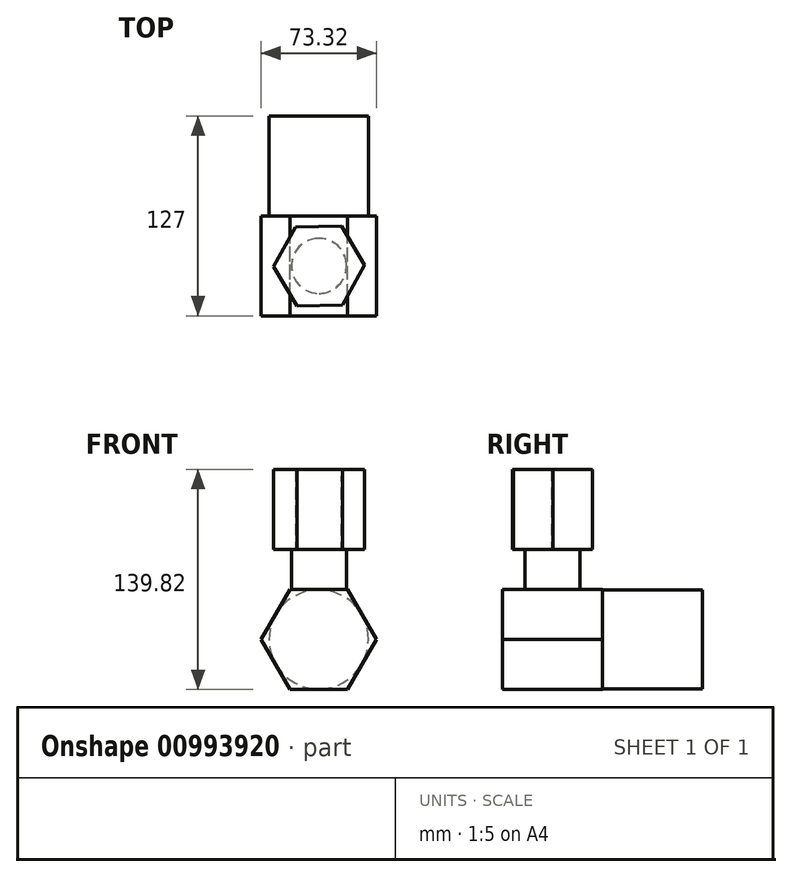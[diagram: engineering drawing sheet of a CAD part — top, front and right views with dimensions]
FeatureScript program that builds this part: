
annotation { "Feature Type Name" : "Feature", "Feature Type Description" : "" }
export const myFeature = defineFeature(function(context is Context, id is Id, definition is map)
    precondition{}
    {
        {
            var Q0;
            Q0=qCreatedBy(makeId("Front.planeOp"),FACE);
            var sketch = newSketch(context, id + "F0", { "sketchPlane" : qUnion([Q0])});
            skCircle(sketch, "E0.cCircle", {"center": v(0, 0) * mm, "radius": 31.75 * mm, "construction": true});
            skLineSegment(sketch, "E0.0", {"start": v(36.66, -0.1) * mm, "end": v(18.25, -31.8) * mm});
            skLineSegment(sketch, "E0.1", {"start": v(18.25, -31.8) * mm, "end": v(-18.4, -31.7) * mm});
            skLineSegment(sketch, "E0.2", {"start": v(-18.4, -31.7) * mm, "end": v(-36.66, 0.1) * mm});
            skLineSegment(sketch, "E0.3", {"start": v(-36.66, 0.1) * mm, "end": v(-18.25, 31.8) * mm});
            skLineSegment(sketch, "E0.4", {"start": v(-18.25, 31.8) * mm, "end": v(18.4, 31.7) * mm});
            skLineSegment(sketch, "E0.5", {"start": v(18.4, 31.7) * mm, "end": v(36.66, -0.1) * mm});
            skPoint(sketch, "E0.0.midPoint", {"position": v(27.46, -15.94) * mm});
            skSolve(sketch);
        }
        {
            var Q0;
            Q0 = qSketchRegion(id + "F0", true);
            extrude(context, id + "F1", {"entities" : qUnion([Q0]), "depth" : 63.5 * mm, "offsetDistance" : 25.4 * mm});
        }
        {
            var Q0;
            Q0=makeQuery(id+"F1.opExtrude","CAP_FACE",FACE,{"disambiguationData":[OSD([sQuery(id+"F0.wireOp",EDGE,"E0.0"),sQuery(id+"F0.wireOp",EDGE,"E0.1"),sQuery(id+"F0.wireOp",EDGE,"E0.2"),sQuery(id+"F0.wireOp",EDGE,"E0.3"),sQuery(id+"F0.wireOp",EDGE,"E0.4"),sQuery(id+"F0.wireOp",EDGE,"E0.5")])],"isStart":true});
            var sketch = newSketch(context, id + "F2", { "sketchPlane" : qUnion([Q0])});
            skCircle(sketch, "E1", {"center": v(0, 0) * mm, "radius": 31.51 * mm});
            skSolve(sketch);
        }
        {
            var Q0;
            Q0 = qSketchRegion(id + "F2", true);
            extrude(context, id + "F3", {"entities" : qUnion([Q0]), "operationType" : NewBodyOperationType.ADD, "depth" : 63.5 * mm, "offsetDistance" : 25.4 * mm});
        }
        {
            var Q0;
            Q0=makeQuery(id+"F1.opExtrude","SWEPT_FACE",FACE,{"disambiguationData":[OSD([sQuery(id+"F0.wireOp",EDGE,"E0.4")])]});
            var sketch = newSketch(context, id + "F4", { "sketchPlane" : qUnion([Q0])});
            skCircle(sketch, "E2", {"center": v(0, -31.75) * mm, "radius": 17.53 * mm});
            skPoint(sketch, "E2.centerSnap0", {"position": v(-18.33, -31.75) * mm});
            skPoint(sketch, "E2.centerSnap1", {"position": v(0, 0) * mm});
            skSolve(sketch);
        }
        {
            var Q0;
            Q0 = qSketchRegion(id + "F4", true);
            extrude(context, id + "F5", {"entities" : qUnion([Q0]), "operationType" : NewBodyOperationType.ADD, "depth" : 25.4 * mm, "offsetDistance" : 25.4 * mm});
        }
        {
            var Q0;
            Q0=makeQuery(id+"F5.opExtrude","CAP_FACE",FACE,{"disambiguationData":[OSD([sQuery(id+"F4.wireOp",EDGE,"E2")])],"isStart":false});
            var sketch = newSketch(context, id + "F6", { "sketchPlane" : qUnion([Q0])});
            skCircle(sketch, "E3.cCircle", {"center": v(0, -31.75) * mm, "radius": 25.06 * mm, "construction": true});
            skLineSegment(sketch, "E3.0", {"start": v(28.94, -31.26) * mm, "end": v(14.9, -56.56) * mm});
            skLineSegment(sketch, "E3.1", {"start": v(14.9, -56.56) * mm, "end": v(-14.04, -57.05) * mm});
            skLineSegment(sketch, "E3.2", {"start": v(-14.04, -57.05) * mm, "end": v(-28.94, -32.24) * mm});
            skLineSegment(sketch, "E3.3", {"start": v(-28.94, -32.24) * mm, "end": v(-14.9, -6.94) * mm});
            skLineSegment(sketch, "E3.4", {"start": v(-14.9, -6.94) * mm, "end": v(14.04, -6.45) * mm});
            skLineSegment(sketch, "E3.5", {"start": v(14.04, -6.45) * mm, "end": v(28.94, -31.26) * mm});
            skPoint(sketch, "E3.0.midPoint", {"position": v(21.91, -43.91) * mm});
            skSolve(sketch);
        }
        {
            var Q0;
            Q0 = qSketchRegion(id + "F6", true);
            extrude(context, id + "F7", {"entities" : qUnion([Q0]), "operationType" : NewBodyOperationType.ADD, "depth" : 50.8 * mm, "offsetDistance" : 25.4 * mm});
        }
    });
